# Revit family: FU_Table_Sandler_584A-MT
name_source: partatom
category: Furniture
units: mm (PartAtom-declared; Revit-internal decimal feet)

## family parameters
Always vertical = Yes
Cut with Voids When Loaded = No
OmniClass Number = 23.40.20.00
OmniClass Title = General Furniture and Specialties
Room Calculation Point = No
Shared = No
Work Plane-Based = No

## types (2) — shared parameters
Depth = 497 mm
Description = Table base. Available in powdercoat painted finishes.
Optional upcharge for outdoor version with galvanized-treated frame and adjustable feet.
Height = 1100 mm
Manufacturer = Sandler
Model = 584A MT
Top Elevation = 1100 mm
URL = https://www.sandlerseating.com
Width = 497 mm
zero-valued in all types: Default Elevation

## per-type parameters (varying)
| type | Top Type |
| 584A MT - 32" Square Top (80cm) | FU_TableTops_MT Sqr : 32" Square (80cm) |
| 584A MT - 32" Round Top (80cm) | FU_TableTops_MT Rnd : 32" Round (80cm) |

## geometry (parser evidence)
native form markers: Sweep x14
no freeform markers — native parametric forms only
